# Revit family: HAWLE Гидрант
name_source: partatom
category: Оборудование
revit_build: Autodesk Revit 2017 (Build: 20171027_0315(x64)
units: mm (PartAtom-declared; Revit-internal decimal feet)

## family parameters
Всегда вертикально = Да
На основе рабочей плоскости = Нет
Общий = Нет
При загрузке вырезать с полостями = Нет
Размер круглого соединителя = Использовать диаметр
Тип детали = Нормальный
Точка расчета площади = Нет

## types (13) — shared parameters
ADSK_Единица измерения = Шт.
ADSK_Завод-изготовитель = Hawle
ADSK_Код изделия = 5035
ADSK_Наименование = Подземный гидрант DUO GOST
ADSK_Обозначение = DN100(EN1092-2)
DN = 100 мм
DN_наруж = 57 мм
D_Колено для опорожнения = 15 мм
URL = https://www.hawle.ru
Изготовитель = ООО Хавле-Севком
Изготовитель телефон = +7(812)6707670
Материал_Колено = Hawle_Латунь
Материал_Основание = Hawle_Чугун
Материал_Труба = Hawle_Cталь
Разработчик = ООО ПРОРУБИМ
Разработчик (телефон) = +7(495)649-85-43
Разработчик модели (URL) = http://prorubim.com

## per-type parameters (varying)
| type | ADSK_Масса | ADSK_Масса_Текст | L |
| DUO GOST 750 | 32.5 | 32.5 | 750 мм |
| DUO GOST 1000 | 36.5 | 36.5 | 1000 мм |
| DUO GOST 1250 | 40.5 | 40.5 | 1250 мм |
| DUO GOST 1500 | 45 | 45 | 1500 мм |
| DUO GOST 1750 | 49 | 49 | 1750 мм |
| DUO GOST 2000 | 53 | 53 | 2000 мм |
| DUO GOST 2250 | 58 | 58 | 2250 мм |
| DUO GOST 2500 | 63 | 63 | 2500 мм |
| DUO GOST 2750 | 67 | 67 | 2750 мм |
| DUO GOST 3000 | 71 | 71 | 3000 мм |
| DUO GOST 3250 | 75 | 75 | 3250 мм |
| DUO GOST 3500 | 79 | 79 | 3500 мм |
| DUO GOST 4000 | 83 | 83 | 4000 мм |
